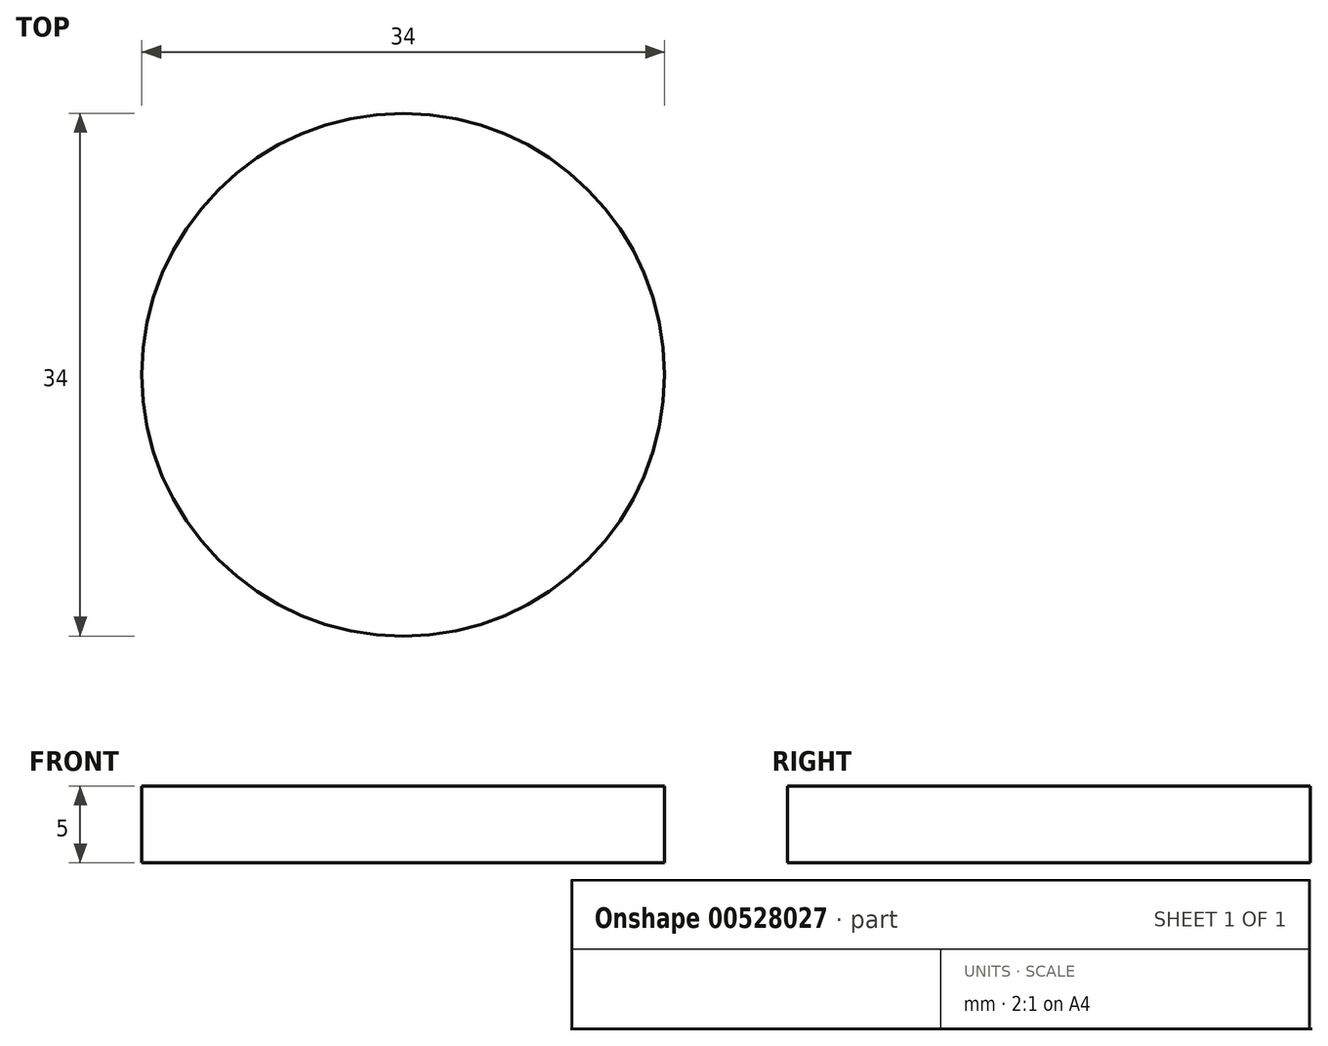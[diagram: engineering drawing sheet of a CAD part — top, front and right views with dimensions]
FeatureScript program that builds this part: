
annotation { "Feature Type Name" : "Feature", "Feature Type Description" : "" }
export const myFeature = defineFeature(function(context is Context, id is Id, definition is map)
    precondition{}
    {
        {
            var Q0;
            Q0=qCreatedBy(makeId("Top.planeOp"),FACE);
            var sketch = newSketch(context, id + "F0", { "sketchPlane" : qUnion([Q0])});
            skCircle(sketch, "E0", {"center": v(0, 0) * mm, "radius": 17 * mm});
            skSolve(sketch);
        }
        {
            var Q0;
            Q0=makeQuery(id+"F0.imprint","IMPRINT",FACE,{"disambiguationData":[TD([[makeQuery(id+"F0.imprint","IMPRINT",EDGE,{"derivedFrom":sQuery(id+"F0.wireOp",EDGE,"E0")}),1.0]])]});
            extrude(context, id + "F1", {"entities" : qUnion([Q0]), "depth" : 5 * mm, "offsetDistance" : 25 * mm});
        }
    });
